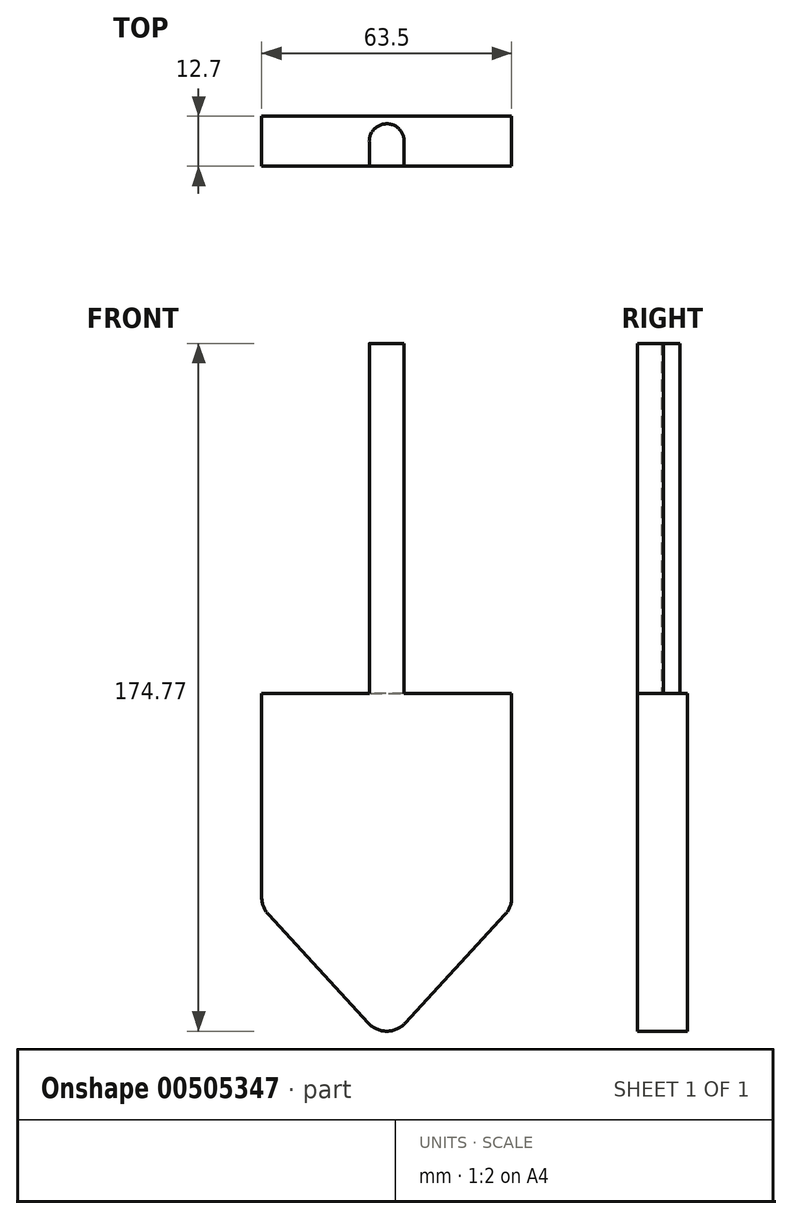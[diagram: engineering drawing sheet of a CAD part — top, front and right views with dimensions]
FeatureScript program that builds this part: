
annotation { "Feature Type Name" : "Feature", "Feature Type Description" : "" }
export const myFeature = defineFeature(function(context is Context, id is Id, definition is map)
    precondition{}
    {
        {
            var Q0;
            Q0=qCreatedBy(makeId("Front.planeOp"),FACE);
            var sketch = newSketch(context, id + "F0", { "sketchPlane" : qUnion([Q0])});
            skLineSegment(sketch, "E0", {"start": v(-31.75, 37.17) * mm, "end": v(31.75, 37.17) * mm});
            skLineSegment(sketch, "E1", {"start": v(31.75, 37.17) * mm, "end": v(31.75, -14.71) * mm});
            skLineSegment(sketch, "E2", {"start": v(30.08, -19.01) * mm, "end": v(4.68, -46.65) * mm});
            skLineSegment(sketch, "E3", {"start": v(-4.68, -46.65) * mm, "end": v(-30.08, -19.01) * mm});
            skLineSegment(sketch, "E4", {"start": v(-31.75, -14.71) * mm, "end": v(-31.75, 37.17) * mm});
            skPoint(sketch, "E5.visualSharp", {"position": v(-31.75, -17.19) * mm});
            skArc(sketch, "E5.filletArc", {"start": v(-31.75, -14.71) * mm, "mid": v(-31.32, -17.02) * mm, "end": v(-30.08, -19.01) * mm});
            skPoint(sketch, "E6.visualSharp", {"position": v(31.75, -17.19) * mm});
            skArc(sketch, "E6.filletArc", {"start": v(30.08, -19.01) * mm, "mid": v(31.32, -17.02) * mm, "end": v(31.75, -14.71) * mm});
            skPoint(sketch, "E7.visualSharp", {"position": v(0, -51.73) * mm});
            skArc(sketch, "E7.filletArc", {"start": v(-4.68, -46.65) * mm, "mid": v(0, -48.7) * mm, "end": v(4.68, -46.65) * mm});
            skSolve(sketch);
        }
        {
            var Q0;
            Q0=makeQuery(id+"F0.imprint","IMPRINT",FACE,{"disambiguationData":[TD([[makeQuery(id+"F0.imprint","IMPRINT",EDGE,{"derivedFrom":sQuery(id+"F0.wireOp",EDGE,"E0")}),-1.0]])]});
            extrude(context, id + "F1", {"entities" : qUnion([Q0]), "depth" : 12.7 * mm});
        }
        {
            var Q0;
            Q0=makeQuery(id+"F1.opExtrude","SWEPT_FACE",FACE,{"disambiguationData":[OSD([sQuery(id+"F0.wireOp",EDGE,"E0")])]});
            var sketch = newSketch(context, id + "F2", { "sketchPlane" : qUnion([Q0])});
            skPoint(sketch, "E8.0", {"position": v(-31.75, -6.35) * mm});
            skLineSegment(sketch, "E9.0", {"start": v(-31.75, -12.7) * mm, "end": v(-31.75, 0) * mm});
            skLineSegment(sketch, "E10.0", {"start": v(31.75, -12.7) * mm, "end": v(31.75, 0) * mm});
            skLineSegment(sketch, "E11.0", {"start": v(-31.75, 0) * mm, "end": v(31.75, 0) * mm});
            skLineSegment(sketch, "E12.0", {"start": v(-31.75, -12.7) * mm, "end": v(31.75, -12.7) * mm});
            skCircle(sketch, "E13", {"center": v(0, -6.35) * mm, "radius": 4.44 * mm});
            skLineSegment(sketch, "E14", {"start": v(-4.43, -6.6) * mm, "end": v(-4.43, -12.7) * mm});
            skLineSegment(sketch, "E15", {"start": v(4.44, -6.2) * mm, "end": v(4.44, -12.7) * mm});
            skLineSegment(sketch, "E16", {"start": v(4.44, -12.7) * mm, "end": v(-4.43, -12.7) * mm});
            skSolve(sketch);
        }
        {
            var Q0;
            {var subQ0=sQuery(id+"F2.wireOp",EDGE,"E14");Q0=makeQuery(id+"F2.imprint","IMPRINT",FACE,{"disambiguationData":[TD([[makeQuery(id+"F2.imprint","IMPRINT",EDGE,{"derivedFrom":subQ0}),1.0]])]});}
            var Q1;
            {var subQ0=sQuery(id+"F2.wireOp",EDGE,"E13");var subQ1=makeQuery(id+"F2.imprint","INTERSECT",VERTEX,{"derivedFrom":[subQ0,sQuery(id+"F2.wireOp",EDGE,"E14")]});Q1=makeQuery(id+"F2.imprint","IMPRINT",FACE,{"disambiguationData":[TD([[makeQuery(id+"F2.imprint","IMPRINT",EDGE,{"disambiguationData":[TD([[subQ1,1.0]])],"derivedFrom":subQ0}),1.0]])]});}
            extrude(context, id + "F3", {"entities" : qUnion([Q0, Q1]), "operationType" : NewBodyOperationType.ADD, "depth" : 88.9 * mm});
        }
    });
